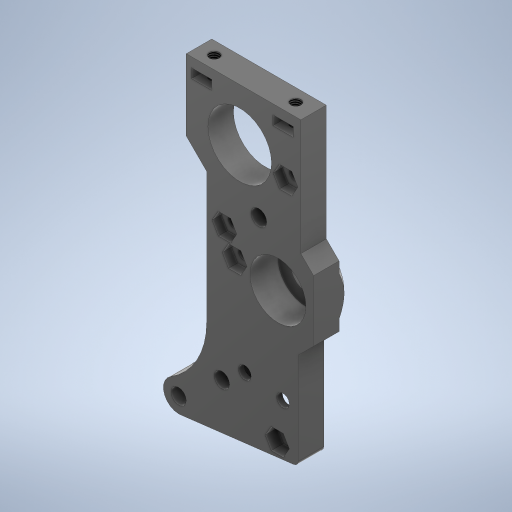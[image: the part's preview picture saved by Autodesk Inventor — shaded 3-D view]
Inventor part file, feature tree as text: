
AUTODESK INVENTOR PART (.ipt)
format: ipt  version: 2023 (Build 270158000, 158)  size: 777,216 bytes
history: native  units: mm
features: extrude x17, sketch x13, fillet x5, projected_geometry x5, thread x2, chamfer x2, other x2, mirror x1, reference x1
ambient origin geometry x8: Origin, YZ Plane, XZ Plane, XY Plane, X Axis, Y Axis, Z Axis, Center Point
bodies: Solid1 (feature_tree)
feature tree (48):
  extrude  "Extrusion1"  Depth=3.0mm
  fillet  "Fillet1"  Radius=23.5mm
  fillet  "Fillet2"  Radius=6.0mm
  extrude  "Extrusion2"  Depth=3.0mm
  extrude  "Extrusion3"  Depth=56.0mm
  thread  "Thread1"  [1 undecoded]
  thread  "Thread2"  [1 undecoded]
  extrude  "Extrusion4"  Depth=12.5mm
  extrude  "Extrusion5"  Depth=2.1mm
  extrude  "Extrusion6"  Depth=4.0mm
  extrude  "Extrusion7"  TaperAngle=45.0deg  [1 undecoded]
  extrude  "Extrusion8"  Depth=3.0mm
  extrude  "Extrusion9"  TaperAngle=135.0deg  [1 undecoded]
  extrude  "Extrusion10"  Depth=3.0mm TaperAngle=0.0deg
  fillet  "Fillet3"  Radius=3.0mm
  extrude  "Extrusion11"  Depth=3.0mm
  chamfer  "Chamfer1"  Distance=7.5mm
  fillet  "Fillet4"  Radius=2.5mm
  extrude  "Extrusion12"  Depth=10.0mm
  extrude  "Extrusion13"  Depth=10.0mm
  extrude  "Extrusion14"  Depth=1.0mm
  fillet  "Fillet5"  Radius=15.0mm
  mirror  "Mirror2"
  extrude  "Extrusion15"  Depth=10.0mm
  chamfer  "Chamfer2"  Distance=20.0mm
  extrude  "Extrusion16"  Depth=10.0mm
  extrude  "Extrusion17"  Depth=3.0mm TaperAngle=0.0deg
  sketch  "Sketch3"  dims[d0=3.0mm d1=6.0mm d2=23.5mm d3=6.0mm]
  projected_geometry  "Projected Loop1"
  sketch  "Sketch5"  dims[d4=0.0mm d5=3.0mm]
  sketch  "Sketch7"  dims[d6=18.0mm d7=56.0mm d8=11.0mm d9=4.0mm]
  sketch  "Sketch8"  dims[d10=24.75mm d11=12.5mm]
  projected_geometry  "Projected Loop2"
  sketch  "Sketch10"  dims[d12=22.3mm d14=2.1mm]
  sketch  "Sketch13"  dims[d18=30.0mm d20=360.0deg d22=4.0mm]
  sketch  "Sketch15"  dims[d23=14.0mm d24=45.0deg]
  sketch  "Sketch17"  dims[d25=3.0mm d26=12.0mm]
  projected_geometry  "Projected Loop3"
  sketch  "Sketch21"  dims[d27=6.0mm d28=135.0deg]
  projected_geometry  "Projected Loop5"
  sketch  "Sketch22"  dims[d29=135.0deg d30=5.0mm d31=0.0mm d32=3.0mm]
  projected_geometry  "Projected Loop6"
  sketch  "Sketch24"  dims[d33=10.0mm d34=3.0mm]
  sketch  "Sketch25"  dims[d35=2.5mm]
  sketch  "Sketch26"  dims[d36=13.5mm d37=7.5mm d38=2.5mm d39=15.0mm d40=12.5mm d41=1.0mm d42=15.0mm d43=12.75mm d44=20.0mm d45=23.75mm d46=3.0mm d47=0.0mm d48=2.0mm d49=2.0mm d50=2.5mm d51=2.5mm d52=3.0mm d53=3.0mm d54=4.5mm d55=0.0mm d56=7.0mm d57=0.0mm d58=7.0mm d59=0.0mm d60=8.5mm d61=270.0deg d62=4.0mm d63=4.0mm d64=4.0mm d65=3.0mm d66=0.0mm d67=5.5mm d68=2.0mm d69=0.0mm d70=4.0mm d71=1.85mm d72=4.0mm d73=1.85mm d74=1.0mm d75=2.8mm d76=2.8mm d77=1.0mm d78=10.0mm d79=0.0mm d82=3.1mm d83=11.15mm d84=2.1mm d85=2.1mm d86=2.1mm d87=5.5mm d88=3.5mm d89=25.75mm d90=30.25mm d91=2.5mm d92=11.75mm d93=24.0mm d94=8.0mm d95=2.1mm d96=2.1mm d98=2.1mm d99=1.8mm d100=0.0mm d101=2.1mm d102=2.1mm d103=2.1mm d104=1.8mm d105=0.0mm d117=3.9mm d118=0.0mm d119=18.0mm d120=6.5mm d121=0.0mm d122=1.0mm d125=5.0mm d126=7.25mm d127=2.5mm d128=5.0mm d129=15.0mm d130=5.0mm d131=5.0mm d132=90.0deg d133=135.0deg d135=135.0deg d136=135.0deg d137=3.0mm d138=0.0mm d139=0.9mm d140=2.0mm d141=45.0deg d142=4.0mm d143=2.0mm d144=2.6mm d145=3.625mm d146=10.0mm d147=0.0mm d148=2.05mm d149=2.4mm d150=0.0mm d151=4.5mm d154=1.0mm d155=0.0mm d156=2.0mm d157=2.8mm d158=1.0mm d159=1.5mm d160=0.0mm d161=1.5mm d162=2.0mm d163=45.0deg d164=6.0mm d165=0.5mm d166=10.0mm d167=0.0mm d168=0.5mm d169=0.0mm d80=0.5mm d81=0.872665mm d106=0.872665mm d123=0.872665mm d134=0.5mm d153=0.5mm]
  reference  "Reference1"
  other  "Dribbler-3-gears-new.iam"
  other  "Kugellager 685-ZZ-C3:2"
note: 4 required parameter values undecoded (feature->parameter linkage not recoverable at this tier; creation-order binding heuristic only, values carry confidence <= 0.55)
